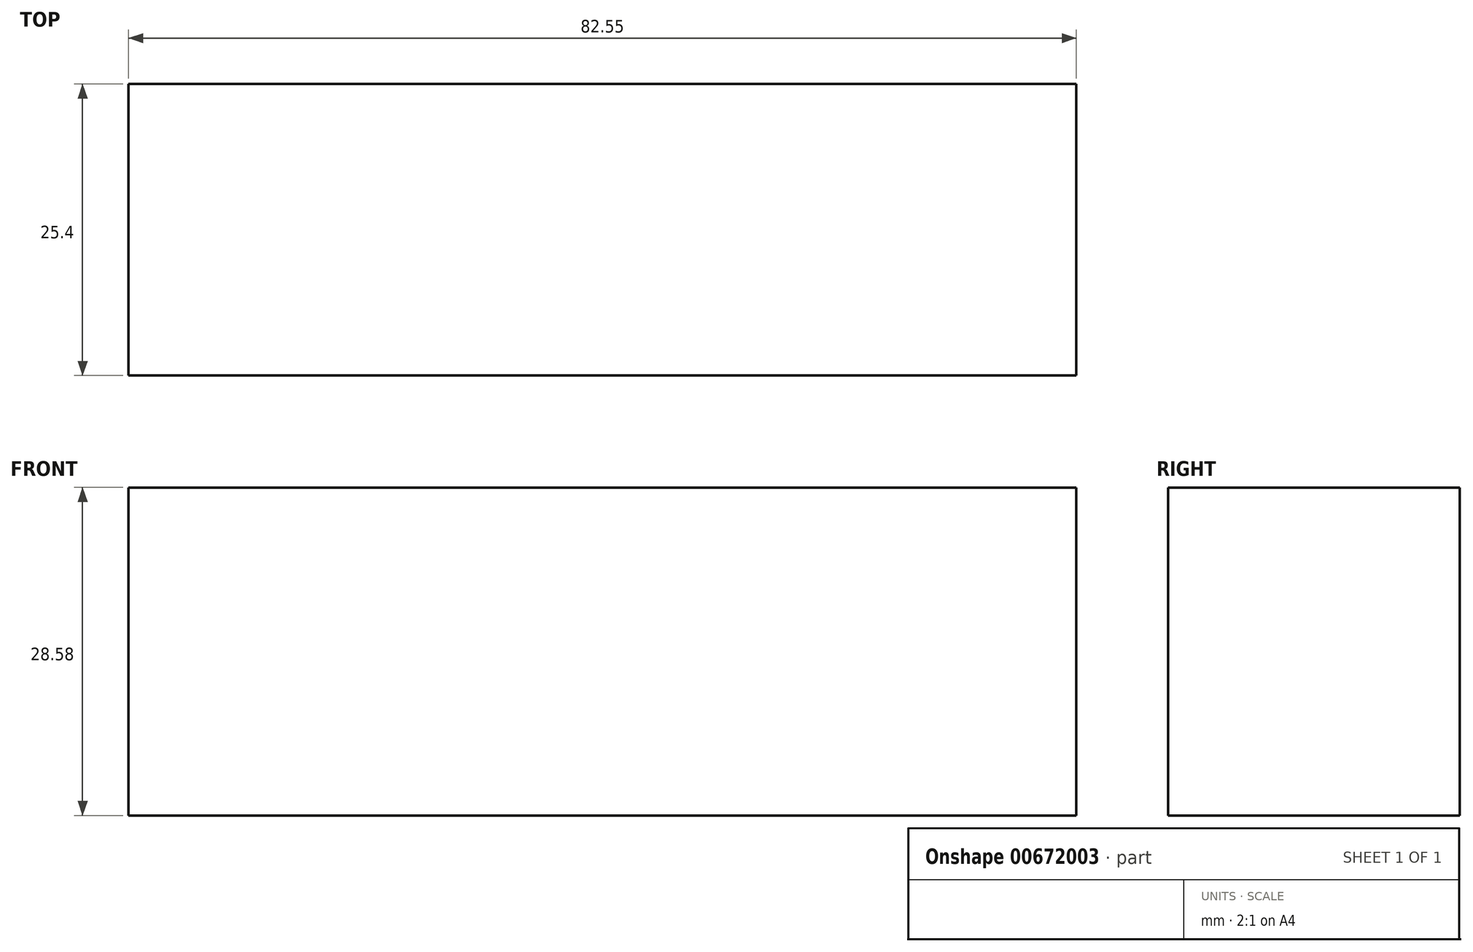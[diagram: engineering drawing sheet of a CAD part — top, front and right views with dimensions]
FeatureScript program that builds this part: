
annotation { "Feature Type Name" : "Feature", "Feature Type Description" : "" }
export const myFeature = defineFeature(function(context is Context, id is Id, definition is map)
    precondition{}
    {
        {
            var Q0;
            Q0=qCreatedBy(makeId("Front.planeOp"),FACE);
            var sketch = newSketch(context, id + "F0", { "sketchPlane" : qUnion([Q0])});
            skLineSegment(sketch, "E0.bottom", {"start": v(41.27, 14.29) * mm, "end": v(-41.28, 14.29) * mm});
            skLineSegment(sketch, "E0.top", {"start": v(41.28, -14.29) * mm, "end": v(-41.27, -14.29) * mm});
            skLineSegment(sketch, "E0.left", {"start": v(41.27, 14.29) * mm, "end": v(41.28, -14.29) * mm});
            skLineSegment(sketch, "E0.right", {"start": v(-41.28, 14.29) * mm, "end": v(-41.27, -14.29) * mm});
            skPoint(sketch, "E0.middle", {"position": v(0, 0) * mm});
            skLineSegment(sketch, "E1.bottom", {"start": v(155.3, 109.67) * mm, "end": v(79.1, 109.67) * mm});
            skLineSegment(sketch, "E1.top", {"start": v(155.3, 46.17) * mm, "end": v(79.1, 46.17) * mm});
            skLineSegment(sketch, "E1.left", {"start": v(155.3, 109.67) * mm, "end": v(155.3, 46.17) * mm});
            skLineSegment(sketch, "E1.right", {"start": v(79.1, 109.67) * mm, "end": v(79.1, 46.17) * mm});
            skPoint(sketch, "E1.middle", {"position": v(117.2, 77.92) * mm});
            skLineSegment(sketch, "E2", {"start": v(41.27, 14.29) * mm, "end": v(41.27, 45.68) * mm});
            skArc(sketch, "E3", {"start": v(41.27, 45.68) * mm, "mid": v(46.63, 58.92) * mm, "end": v(59.67, 64.72) * mm});
            skLineSegment(sketch, "E4", {"start": v(59.67, 64.72) * mm, "end": v(97.77, 64.72) * mm});
            skLineSegment(sketch, "E5.0", {"start": v(59.4, 83.77) * mm, "end": v(97.74, 83.77) * mm});
            skArc(sketch, "E5.1", {"start": v(22.22, 45.68) * mm, "mid": v(33.06, 72.3) * mm, "end": v(59.4, 83.77) * mm});
            skLineSegment(sketch, "E5.2", {"start": v(22.22, 14.29) * mm, "end": v(22.22, 45.68) * mm});
            skLineSegment(sketch, "E6", {"start": v(22.22, 45.68) * mm, "end": v(41.27, 45.68) * mm});
            skFitSpline(sketch, "E7", {"points": [v(-41.28, 14.29) * mm, v(78.57, 83.77) * mm], "startDerivative": vector(68.48, 91.2) * mm, "endDerivative": vector(164.77, -9.2) * mm});
            skSolve(sketch);
        }
        {
            var Q0;
            Q0=makeQuery(id+"F0.imprint","IMPRINT",FACE,{"disambiguationData":[TD([[makeQuery(id+"F0.imprint","IMPRINT",EDGE,{"derivedFrom":sQuery(id+"F0.wireOp",EDGE,"E0.top")}),-1.0]])]});
            extrude(context, id + "F1", {"entities" : qUnion([Q0]), "depth" : 25.4 * mm, "offsetDistance" : 25.4 * mm});
        }
    });
